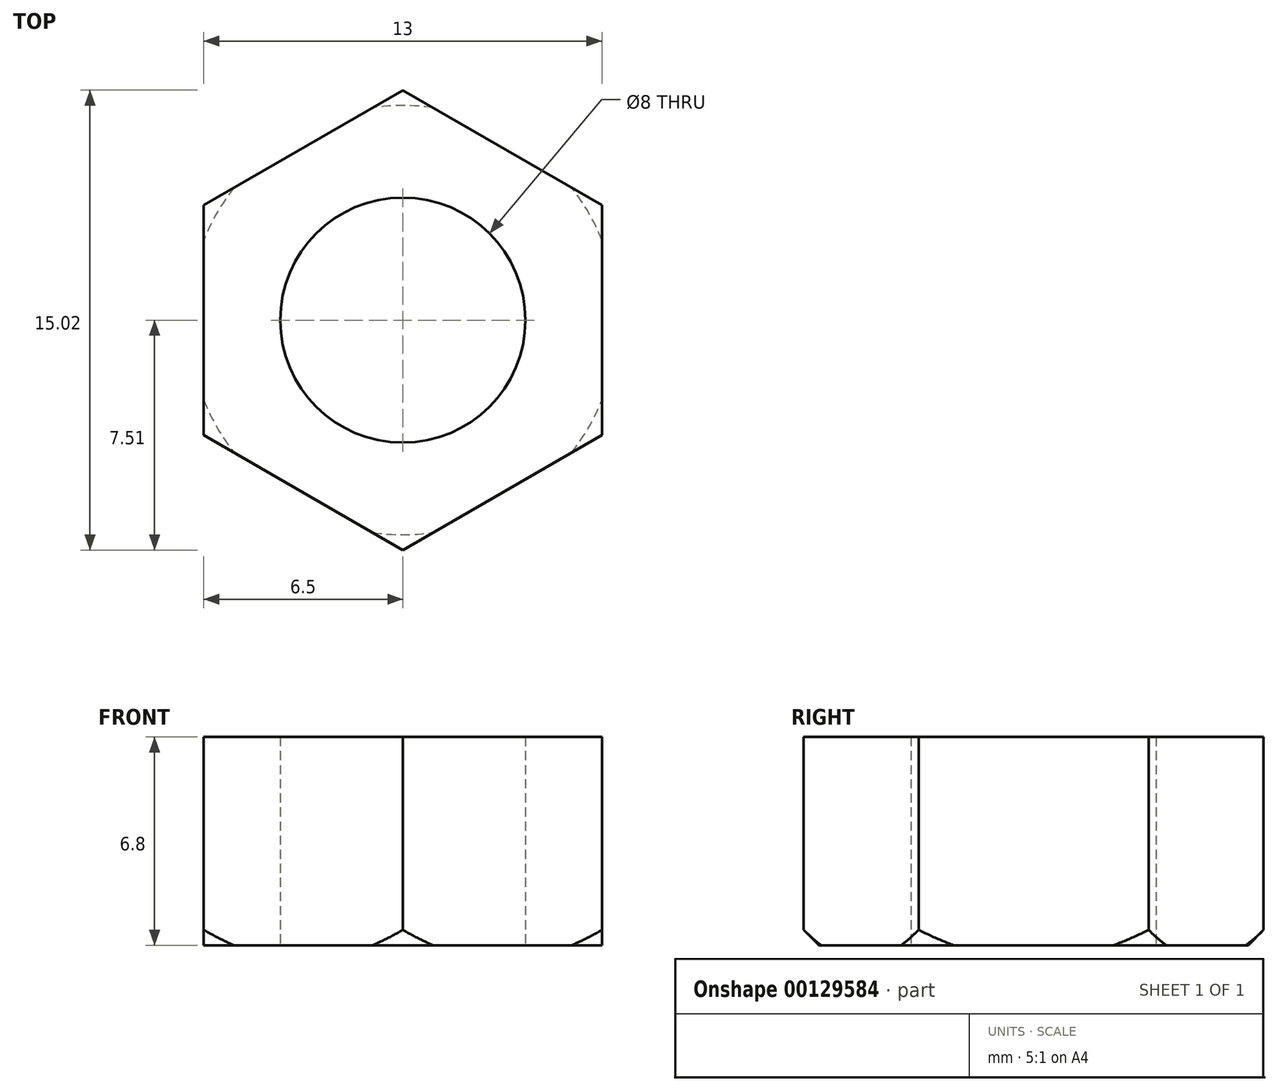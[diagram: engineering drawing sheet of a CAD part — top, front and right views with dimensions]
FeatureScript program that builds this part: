
annotation { "Feature Type Name" : "Feature", "Feature Type Description" : "" }
export const myFeature = defineFeature(function(context is Context, id is Id, definition is map)
    precondition{}
    {
        {
            var Q0;
            Q0=qCreatedBy(makeId("Top.planeOp"),FACE);
            var sketch = newSketch(context, id + "F0", { "sketchPlane" : qUnion([Q0])});
            skCircle(sketch, "E0.cCircle", {"center": v(0, 0) * mm, "radius": 6.5 * mm, "construction": true});
            skLineSegment(sketch, "E0.0", {"start": v(-6.5, -3.75) * mm, "end": v(-6.5, 3.75) * mm});
            skLineSegment(sketch, "E0.1", {"start": v(-6.5, 3.75) * mm, "end": v(0, 7.5) * mm});
            skLineSegment(sketch, "E0.2", {"start": v(0, 7.5) * mm, "end": v(6.5, 3.75) * mm});
            skLineSegment(sketch, "E0.3", {"start": v(6.5, 3.75) * mm, "end": v(6.5, -3.75) * mm});
            skLineSegment(sketch, "E0.4", {"start": v(6.5, -3.75) * mm, "end": v(0, -7.5) * mm});
            skLineSegment(sketch, "E0.5", {"start": v(0, -7.5) * mm, "end": v(-6.5, -3.75) * mm});
            skPoint(sketch, "E0.0.midPoint", {"position": v(-6.5, 0) * mm});
            skCircle(sketch, "E1", {"center": v(0, 0) * mm, "radius": 4 * mm});
            skSolve(sketch);
        }
        {
            var Q0;
            Q0 = qSketchRegion(id + "F0", true);
            extrude(context, id + "F1", {"entities" : qUnion([Q0]), "depth" : 6.8 * mm});
        }
        {
            var Q0;
            Q0=qCreatedBy(makeId("Right.planeOp"),FACE);
            var sketch = newSketch(context, id + "F2", { "sketchPlane" : qUnion([Q0])});
            skLineSegment(sketch, "E2", {"start": v(7.5, 0) * mm, "end": v(7, 0) * mm});
            skLineSegment(sketch, "E3", {"start": v(7, 0) * mm, "end": v(7.5, 0.5) * mm});
            skLineSegment(sketch, "E4", {"start": v(7.5, 0.5) * mm, "end": v(7.5, 0) * mm});
            skSolve(sketch);
        }
        {
            var Q0;
            Q0 = qSketchRegion(id + "F2", true);
            var Q1;
            Q1=makeQuery(id+"F1.opExtrude","SWEPT_FACE",FACE,{"disambiguationData":[OSD([sQuery(id+"F0.wireOp",EDGE,"E1")])]});
            revolve(context, id + "F3", {"operationType" : NewBodyOperationType.REMOVE, "entities" : qUnion([Q0]), "axis" : qUnion([Q1]), "revolveType" : RevolveType.FULL});
        }
    });
